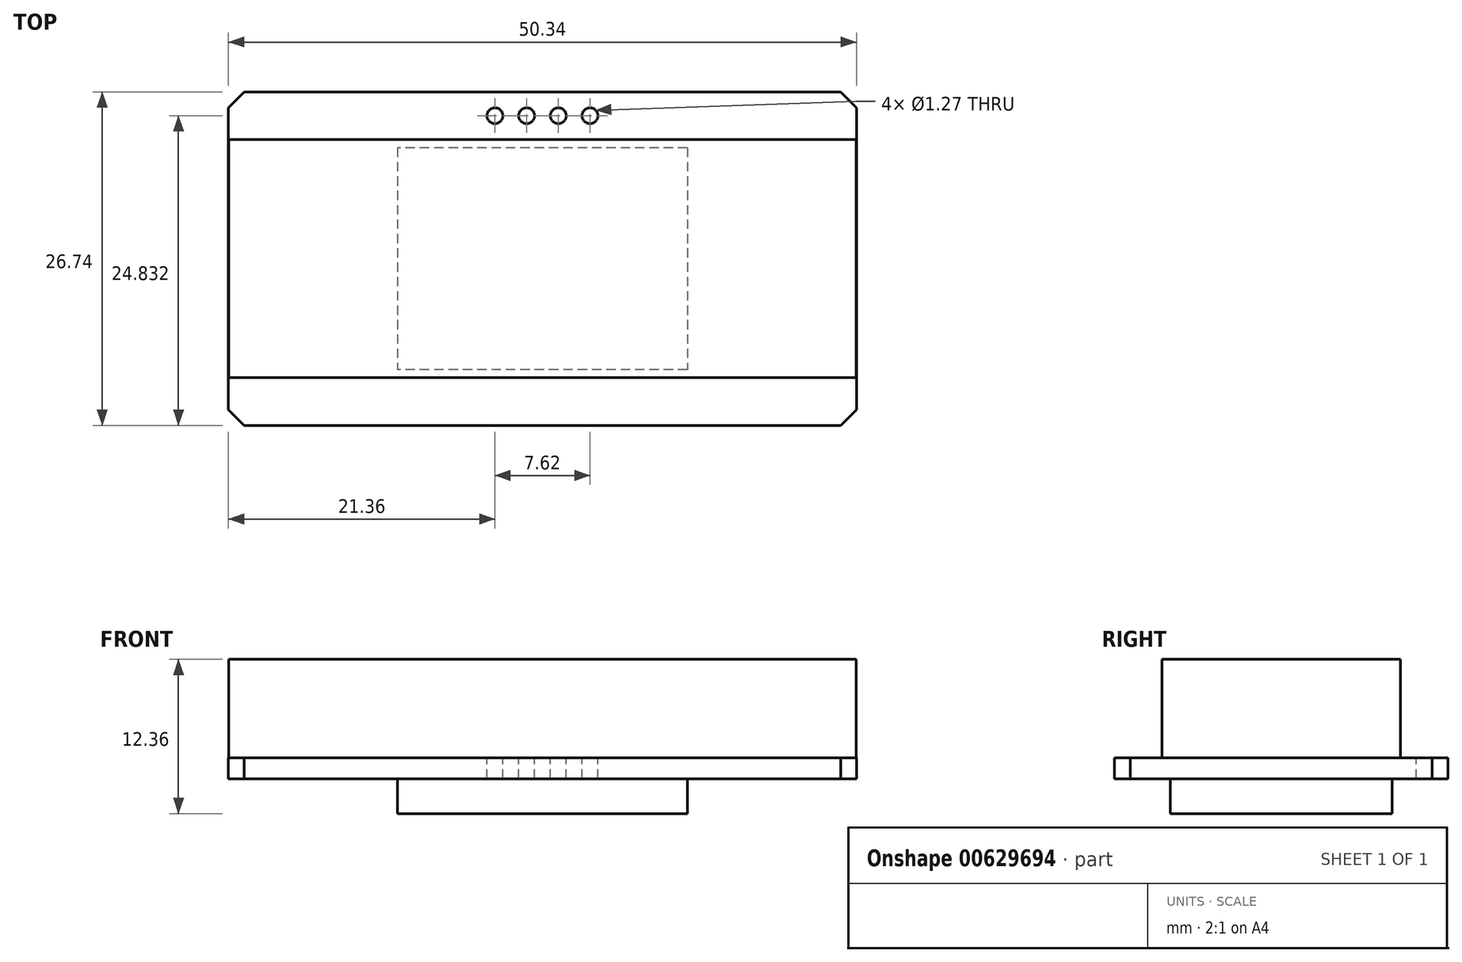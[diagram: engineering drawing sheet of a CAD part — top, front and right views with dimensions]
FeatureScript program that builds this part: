
annotation { "Feature Type Name" : "Feature", "Feature Type Description" : "" }
export const myFeature = defineFeature(function(context is Context, id is Id, definition is map)
    precondition{}
    {
        {
            var Q0;
            Q0=qCreatedBy(makeId("Top.planeOp"),FACE);
            var sketch = newSketch(context, id + "F0", { "sketchPlane" : qUnion([Q0])});
            skLineSegment(sketch, "E0.bottom", {"start": v(25.17, 13.37) * mm, "end": v(-25.17, 13.37) * mm});
            skLineSegment(sketch, "E0.top", {"start": v(25.17, -13.37) * mm, "end": v(-25.17, -13.37) * mm});
            skLineSegment(sketch, "E0.left", {"start": v(25.17, 13.37) * mm, "end": v(25.17, -13.37) * mm});
            skLineSegment(sketch, "E0.right", {"start": v(-25.17, 13.37) * mm, "end": v(-25.17, -13.37) * mm});
            skPoint(sketch, "E0.middle", {"position": v(0, 0) * mm});
            skSolve(sketch);
        }
        {
            var Q0;
            Q0 = qSketchRegion(id + "F0", true);
            extrude(context, id + "F1", {"entities" : qUnion([Q0]), "oppositeDirection" : true, "depth" : 1.68 * mm, "offsetDistance" : 25.4 * mm});
        }
        {
            var Q0;
            Q0=qCreatedBy(makeId("Top.planeOp"),FACE);
            var sketch = newSketch(context, id + "F2", { "sketchPlane" : qUnion([Q0])});
            skLineSegment(sketch, "E1.bottom", {"start": v(25.16, 9.55) * mm, "end": v(-25.16, 9.55) * mm});
            skLineSegment(sketch, "E1.top", {"start": v(25.16, -9.55) * mm, "end": v(-25.16, -9.55) * mm});
            skLineSegment(sketch, "E1.left", {"start": v(25.16, 9.55) * mm, "end": v(25.16, -9.55) * mm});
            skLineSegment(sketch, "E1.right", {"start": v(-25.16, 9.55) * mm, "end": v(-25.16, -9.55) * mm});
            skPoint(sketch, "E1.middle", {"position": v(0, 0) * mm});
            skSolve(sketch);
        }
        {
            var Q0;
            Q0 = qSketchRegion(id + "F2", true);
            extrude(context, id + "F3", {"entities" : qUnion([Q0]), "operationType" : NewBodyOperationType.ADD, "depth" : 7.89 * mm, "offsetDistance" : 25.4 * mm});
        }
        {
            var Q0;
            Q0=makeQuery(id+"F1.opExtrude","CAP_FACE",FACE,{"disambiguationData":[OSD([sQuery(id+"F0.wireOp",EDGE,"E0.bottom"),sQuery(id+"F0.wireOp",EDGE,"E0.top"),sQuery(id+"F0.wireOp",EDGE,"E0.left"),sQuery(id+"F0.wireOp",EDGE,"E0.right")])],"isStart":false});
            var sketch = newSketch(context, id + "F4", { "sketchPlane" : qUnion([Q0])});
            skLineSegment(sketch, "E2.bottom", {"start": v(11.62, -8.89) * mm, "end": v(-11.62, -8.9) * mm});
            skLineSegment(sketch, "E2.top", {"start": v(11.62, 8.9) * mm, "end": v(-11.62, 8.89) * mm});
            skLineSegment(sketch, "E2.left", {"start": v(11.62, -8.9) * mm, "end": v(11.62, 8.9) * mm});
            skLineSegment(sketch, "E2.right", {"start": v(-11.62, -8.9) * mm, "end": v(-11.62, 8.89) * mm});
            skPoint(sketch, "E2.middle", {"position": v(0, 0) * mm});
            skSolve(sketch);
        }
        {
            var Q0;
            Q0 = qSketchRegion(id + "F4", true);
            extrude(context, id + "F5", {"entities" : qUnion([Q0]), "operationType" : NewBodyOperationType.ADD, "depth" : 2.8 * mm, "offsetDistance" : 25.4 * mm});
        }
        {
            var Q0;
            Q0=qCreatedBy(makeId("Top.planeOp"),FACE);
            var sketch = newSketch(context, id + "F6", { "sketchPlane" : qUnion([Q0])});
            skLineSegment(sketch, "E3", {"start": v(-3.81, 11.46) * mm, "end": v(-1.27, 11.46) * mm, "construction": true});
            skLineSegment(sketch, "E4", {"start": v(-1.27, 11.46) * mm, "end": v(1.27, 11.46) * mm, "construction": true});
            skLineSegment(sketch, "E5", {"start": v(1.27, 11.46) * mm, "end": v(3.8, 11.46) * mm, "construction": true});
            skLineSegment(sketch, "E6", {"start": v(0, 0) * mm, "end": v(0, 11.46) * mm, "construction": true});
            skCircle(sketch, "E7", {"center": v(-3.81, 11.46) * mm, "radius": 0.64 * mm});
            skCircle(sketch, "E8", {"center": v(-1.27, 11.46) * mm, "radius": 0.64 * mm});
            skCircle(sketch, "E9", {"center": v(1.27, 11.46) * mm, "radius": 0.64 * mm});
            skCircle(sketch, "E10", {"center": v(3.8, 11.46) * mm, "radius": 0.64 * mm});
            skSolve(sketch);
        }
        {
            var Q0;
            Q0 = qSketchRegion(id + "F6", true);
            extrude(context, id + "F7", {"entities" : qUnion([Q0]), "operationType" : NewBodyOperationType.REMOVE, "oppositeDirection" : true, "depth" : 25.4 * mm, "offsetDistance" : 25.4 * mm});
        }
        {
            var Q0;
            Q0=makeQuery(id+"F1.opExtrude","SWEPT_EDGE",EDGE,{"disambiguationData":[OSD([sQuery(id+"F0.wireOp",EDGE,"E0.bottom"),sQuery(id+"F0.wireOp",EDGE,"E0.left")])]});
            var Q1;
            Q1=makeQuery(id+"F1.opExtrude","SWEPT_EDGE",EDGE,{"disambiguationData":[OSD([sQuery(id+"F0.wireOp",EDGE,"E0.top"),sQuery(id+"F0.wireOp",EDGE,"E0.left")])]});
            var Q2;
            Q2=makeQuery(id+"F1.opExtrude","SWEPT_EDGE",EDGE,{"disambiguationData":[OSD([sQuery(id+"F0.wireOp",EDGE,"E0.top"),sQuery(id+"F0.wireOp",EDGE,"E0.right")])]});
            var Q3;
            Q3=makeQuery(id+"F1.opExtrude","SWEPT_EDGE",EDGE,{"disambiguationData":[OSD([sQuery(id+"F0.wireOp",EDGE,"E0.bottom"),sQuery(id+"F0.wireOp",EDGE,"E0.right")])]});
            chamfer(context, id + "F8", {"entities" : qUnion([Q0, Q1, Q2, Q3]), "width" : 1.27 * mm, "tangentPropagation" : true});
        }
    });
